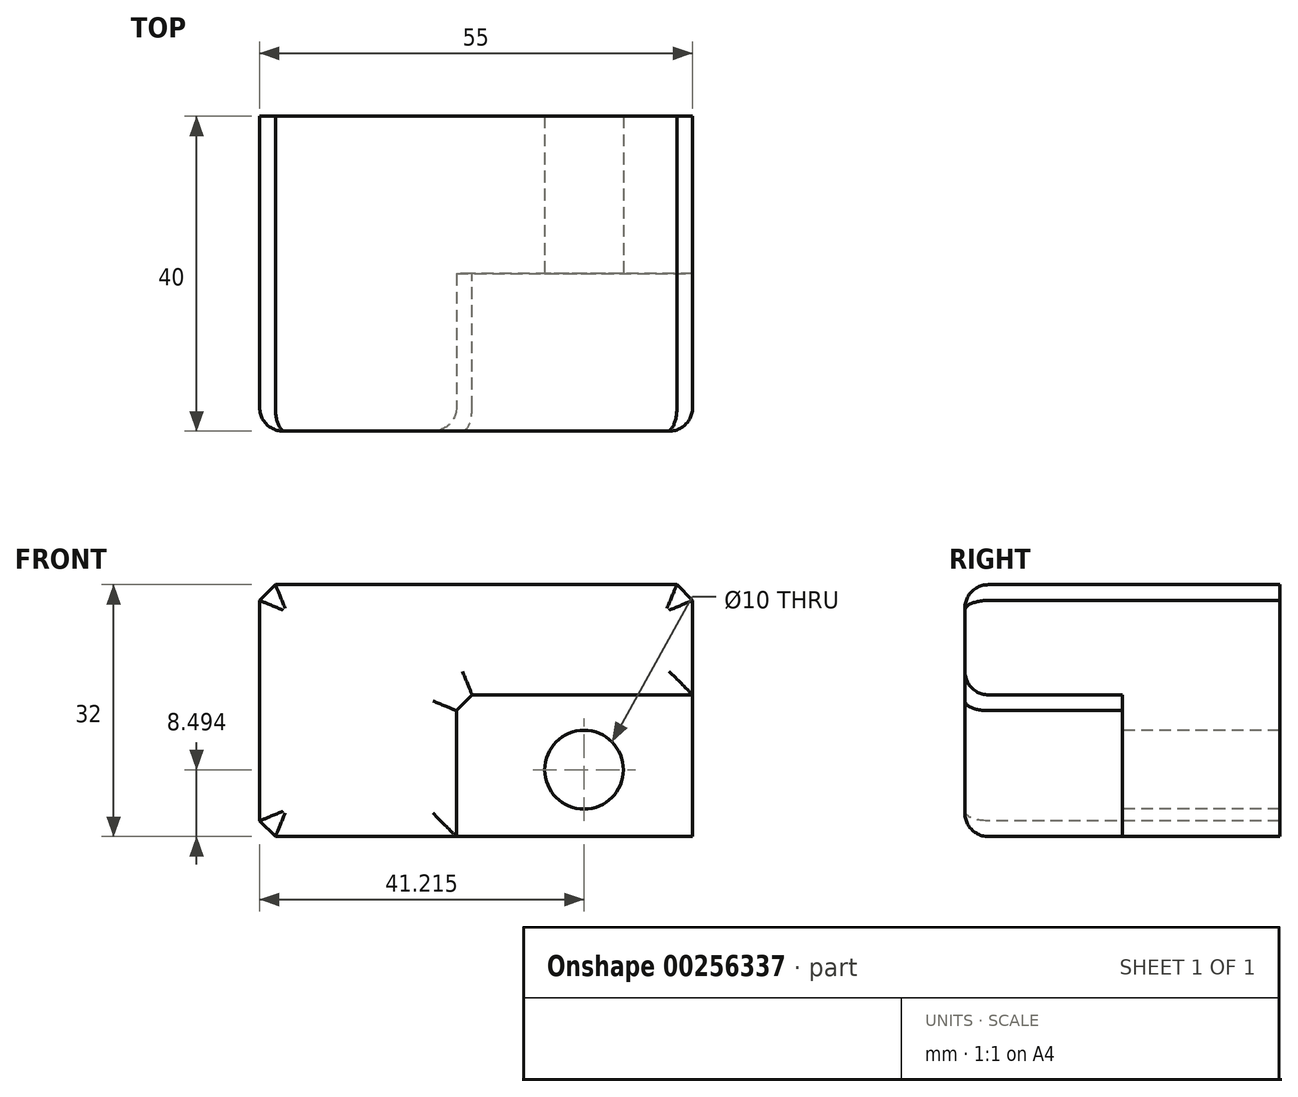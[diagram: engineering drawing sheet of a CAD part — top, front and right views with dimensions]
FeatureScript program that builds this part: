
annotation { "Feature Type Name" : "Feature", "Feature Type Description" : "" }
export const myFeature = defineFeature(function(context is Context, id is Id, definition is map)
    precondition{}
    {
        {
            var Q0;
            Q0=qCreatedBy(makeId("Front.planeOp"),FACE);
            var sketch = newSketch(context, id + "F0", { "sketchPlane" : qUnion([Q0])});
            skLineSegment(sketch, "E0.bottom", {"start": v(0, 0) * mm, "end": v(55, 0) * mm});
            skLineSegment(sketch, "E0.top", {"start": v(0, -32) * mm, "end": v(55, -32) * mm});
            skLineSegment(sketch, "E0.left", {"start": v(0, 0) * mm, "end": v(0, -32) * mm});
            skLineSegment(sketch, "E0.right", {"start": v(55, 0) * mm, "end": v(55, -32) * mm});
            skSolve(sketch);
        }
        {
            var Q0;
            Q0=makeQuery(id+"F0.imprint","IMPRINT",FACE,{"disambiguationData":[TD([[makeQuery(id+"F0.imprint","IMPRINT",EDGE,{"derivedFrom":sQuery(id+"F0.wireOp",EDGE,"E0.bottom")}),-1.0]])]});
            extrude(context, id + "F1", {"entities" : qUnion([Q0]), "depth" : 40 * mm});
        }
        {
            var Q0;
            Q0=makeQuery(id+"F1.opExtrude","CAP_FACE",FACE,{"disambiguationData":[OSD([sQuery(id+"F0.wireOp",EDGE,"E0.bottom"),sQuery(id+"F0.wireOp",EDGE,"E0.top"),sQuery(id+"F0.wireOp",EDGE,"E0.left"),sQuery(id+"F0.wireOp",EDGE,"E0.right")])],"isStart":false});
            var sketch = newSketch(context, id + "F2", { "sketchPlane" : qUnion([Q0])});
            skLineSegment(sketch, "E1.bottom", {"start": v(55, -32) * mm, "end": v(25, -32) * mm});
            skLineSegment(sketch, "E1.top", {"start": v(55, -14) * mm, "end": v(25, -14) * mm});
            skLineSegment(sketch, "E1.left", {"start": v(55, -32) * mm, "end": v(55, -14) * mm});
            skLineSegment(sketch, "E1.right", {"start": v(25, -32) * mm, "end": v(25, -14) * mm});
            skSolve(sketch);
        }
        {
            var Q0;
            Q0=makeQuery(id+"F2.imprint","IMPRINT",FACE,{"disambiguationData":[TD([[makeQuery(id+"F2.imprint","IMPRINT",EDGE,{"derivedFrom":sQuery(id+"F2.wireOp",EDGE,"E1.bottom")}),1.0]])]});
            extrude(context, id + "F3", {"entities" : qUnion([Q0]), "operationType" : NewBodyOperationType.REMOVE, "oppositeDirection" : true, "depth" : 20 * mm});
        }
        {
            var Q0;
            Q0=makeQuery(id+"F3.boolean.opBoolean","COPY",FACE,{"derivedFrom":makeQuery(id+"F3.opExtrude","CAP_FACE",FACE,{"disambiguationData":[OSD([sQuery(id+"F2.wireOp",EDGE,"E1.bottom"),sQuery(id+"F2.wireOp",EDGE,"E1.top"),sQuery(id+"F2.wireOp",EDGE,"E1.left"),sQuery(id+"F2.wireOp",EDGE,"E1.right")])],"isStart":false})});
            var sketch = newSketch(context, id + "F4", { "sketchPlane" : qUnion([Q0])});
            skCircle(sketch, "E2", {"center": v(41.21, -23.5) * mm, "radius": 5 * mm});
            skSolve(sketch);
        }
        {
            var Q0;
            Q0 = qSketchRegion(id + "F4", true);
            extrude(context, id + "F5", {"entities" : qUnion([Q0]), "operationType" : NewBodyOperationType.REMOVE, "endBound" : BoundingType.THROUGH_ALL, "oppositeDirection" : true, "depth" : 25 * mm});
        }
        {
            var Q0;
            Q0=makeQuery(id+"F1.opExtrude","SWEPT_EDGE",EDGE,{"disambiguationData":[OSD([sQuery(id+"F0.wireOp",EDGE,"E0.top"),sQuery(id+"F0.wireOp",EDGE,"E0.left")])]});
            var Q1;
            Q1=makeQuery(id+"F3.boolean.opBoolean","COPY",EDGE,{"derivedFrom":makeQuery(id+"F3.opExtrude","SWEPT_EDGE",EDGE,{"disambiguationData":[OSD([sQuery(id+"F0.wireOp",EDGE,"E0.top"),sQuery(id+"F2.wireOp",EDGE,"E1.bottom"),sQuery(id+"F2.wireOp",EDGE,"E1.right")])]})});
            var Q2;
            Q2=makeQuery(id+"F3.boolean.opBoolean","COPY",EDGE,{"derivedFrom":makeQuery(id+"F3.opExtrude","SWEPT_EDGE",EDGE,{"disambiguationData":[OSD([sQuery(id+"F2.wireOp",EDGE,"E1.top"),sQuery(id+"F2.wireOp",EDGE,"E1.right")])]})});
            var Q3;
            Q3=makeQuery(id+"F1.opExtrude","SWEPT_EDGE",EDGE,{"disambiguationData":[OSD([sQuery(id+"F0.wireOp",EDGE,"E0.bottom"),sQuery(id+"F0.wireOp",EDGE,"E0.right")])]});
            var Q4;
            Q4=makeQuery(id+"F3.boolean.opBoolean","COPY",EDGE,{"derivedFrom":makeQuery(id+"F3.opExtrude","SWEPT_EDGE",EDGE,{"disambiguationData":[OSD([sQuery(id+"F0.wireOp",EDGE,"E0.right"),sQuery(id+"F2.wireOp",EDGE,"E1.top"),sQuery(id+"F2.wireOp",EDGE,"E1.left")])]})});
            var Q5;
            Q5=makeQuery(id+"F1.opExtrude","SWEPT_EDGE",EDGE,{"disambiguationData":[OSD([sQuery(id+"F0.wireOp",EDGE,"E0.bottom"),sQuery(id+"F0.wireOp",EDGE,"E0.left")])]});
            chamfer(context, id + "F6", {"entities" : qUnion([Q0, Q1, Q2, Q3, Q4, Q5]), "width" : 2 * mm, "tangentPropagation" : true});
        }
        {
            var Q0;
            Q0=makeQuery(id+"F3.boolean.opBoolean","COPY",EDGE,{"derivedFrom":makeQuery(id+"F3.opExtrude","CAP_EDGE",EDGE,{"disambiguationData":[OSD([sQuery(id+"F2.wireOp",EDGE,"E1.right")])],"isStart":true})});
            var Q1;
            {var subQ0=sQuery(id+"F0.wireOp",EDGE,"E0.top");Q1=makeQuery(id+"F6.opChamfer","BLEND_EDGE",EDGE,{"blendedFrom":[makeQuery(id+"F3.boolean.opBoolean","COPY",EDGE,{"derivedFrom":makeQuery(id+"F3.opExtrude","SWEPT_EDGE",EDGE,{"disambiguationData":[OSD([subQ0,sQuery(id+"F2.wireOp",EDGE,"E1.bottom"),sQuery(id+"F2.wireOp",EDGE,"E1.right")])]})}),makeQuery(id+"F1.opExtrude","CAP_FACE",FACE,{"disambiguationData":[OSD([sQuery(id+"F0.wireOp",EDGE,"E0.bottom"),subQ0,sQuery(id+"F0.wireOp",EDGE,"E0.left"),sQuery(id+"F0.wireOp",EDGE,"E0.right")])],"isStart":false})],"blendedInto":[makeQuery(id+"F1.opExtrude","CAP_FACE",FACE,{"disambiguationData":[OSD([sQuery(id+"F0.wireOp",EDGE,"E0.bottom"),subQ0,sQuery(id+"F0.wireOp",EDGE,"E0.left"),sQuery(id+"F0.wireOp",EDGE,"E0.right")])],"isStart":false})]});}
            var Q2;
            Q2=makeQuery(id+"F1.opExtrude","CAP_EDGE",EDGE,{"disambiguationData":[OSD([sQuery(id+"F0.wireOp",EDGE,"E0.top")])],"isStart":false});
            var Q3;
            Q3=makeQuery(id+"F1.opExtrude","CAP_EDGE",EDGE,{"disambiguationData":[OSD([sQuery(id+"F0.wireOp",EDGE,"E0.left")])],"isStart":false});
            var Q4;
            Q4=makeQuery(id+"F1.opExtrude","CAP_FACE",FACE,{"disambiguationData":[OSD([sQuery(id+"F0.wireOp",EDGE,"E0.bottom"),sQuery(id+"F0.wireOp",EDGE,"E0.top"),sQuery(id+"F0.wireOp",EDGE,"E0.left"),sQuery(id+"F0.wireOp",EDGE,"E0.right")])],"isStart":false});
            var Q5;
            Q5=makeQuery(id+"F3.boolean.opBoolean","COPY",EDGE,{"derivedFrom":makeQuery(id+"F3.opExtrude","CAP_EDGE",EDGE,{"disambiguationData":[OSD([sQuery(id+"F2.wireOp",EDGE,"E1.top")])],"isStart":true})});
            fillet(context, id + "F7", {"entities" : qUnion([Q0, Q1, Q2, Q3, Q4, Q5]), "radius" : 3 * mm, "tangentPropagation" : true, "allowEdgeOverflow" : false});
        }
    });
